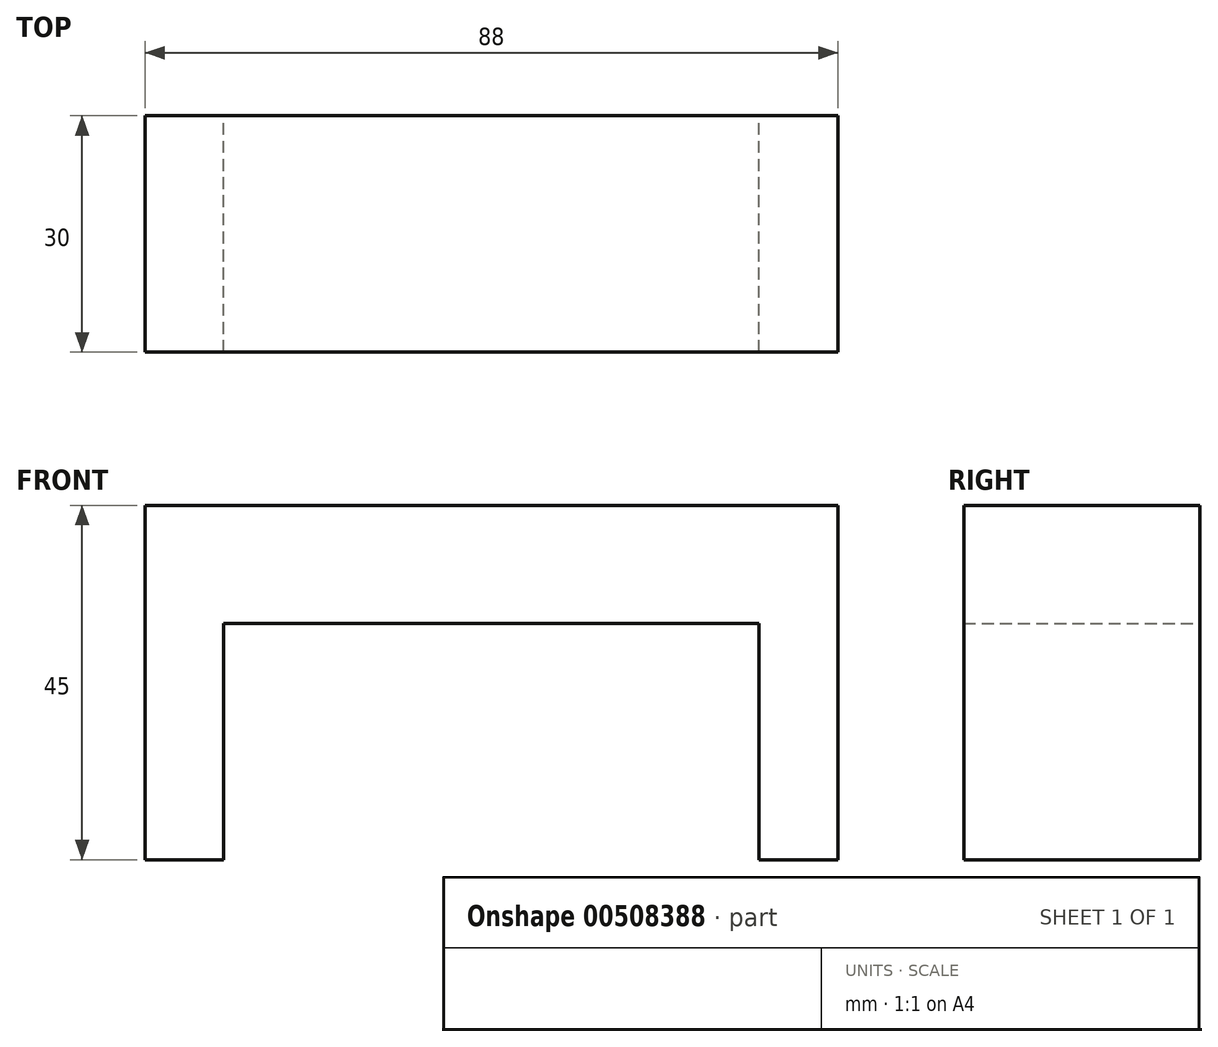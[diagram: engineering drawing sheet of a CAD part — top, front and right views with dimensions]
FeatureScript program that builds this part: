
annotation { "Feature Type Name" : "Feature", "Feature Type Description" : "" }
export const myFeature = defineFeature(function(context is Context, id is Id, definition is map)
    precondition{}
    {
        {
            var Q0;
            Q0=qCreatedBy(makeId("Front.planeOp"),FACE);
            var sketch = newSketch(context, id + "F0", { "sketchPlane" : qUnion([Q0])});
            skLineSegment(sketch, "E0", {"start": v(-27.53, 23.59) * mm, "end": v(40.47, 23.59) * mm});
            skLineSegment(sketch, "E1", {"start": v(-27.53, 23.59) * mm, "end": v(-27.53, -6.41) * mm});
            skLineSegment(sketch, "E2", {"start": v(-27.53, -6.41) * mm, "end": v(-37.53, -6.41) * mm});
            skLineSegment(sketch, "E3", {"start": v(-37.53, -6.41) * mm, "end": v(-37.53, 38.59) * mm});
            skLineSegment(sketch, "E4", {"start": v(-37.53, 38.59) * mm, "end": v(50.47, 38.59) * mm});
            skLineSegment(sketch, "E5", {"start": v(50.47, 38.59) * mm, "end": v(50.47, -6.41) * mm});
            skLineSegment(sketch, "E6", {"start": v(50.47, -6.41) * mm, "end": v(40.47, -6.41) * mm});
            skLineSegment(sketch, "E7", {"start": v(40.47, 23.59) * mm, "end": v(40.47, -6.41) * mm});
            skSolve(sketch);
        }
        {
            var Q0;
            Q0=makeQuery(id+"F0.imprint","IMPRINT",FACE,{"disambiguationData":[TD([[makeQuery(id+"F0.imprint","IMPRINT",EDGE,{"derivedFrom":sQuery(id+"F0.wireOp",EDGE,"E0")}),1.0]])]});
            extrude(context, id + "F1", {"entities" : qUnion([Q0]), "depth" : 30 * mm});
        }
    });
